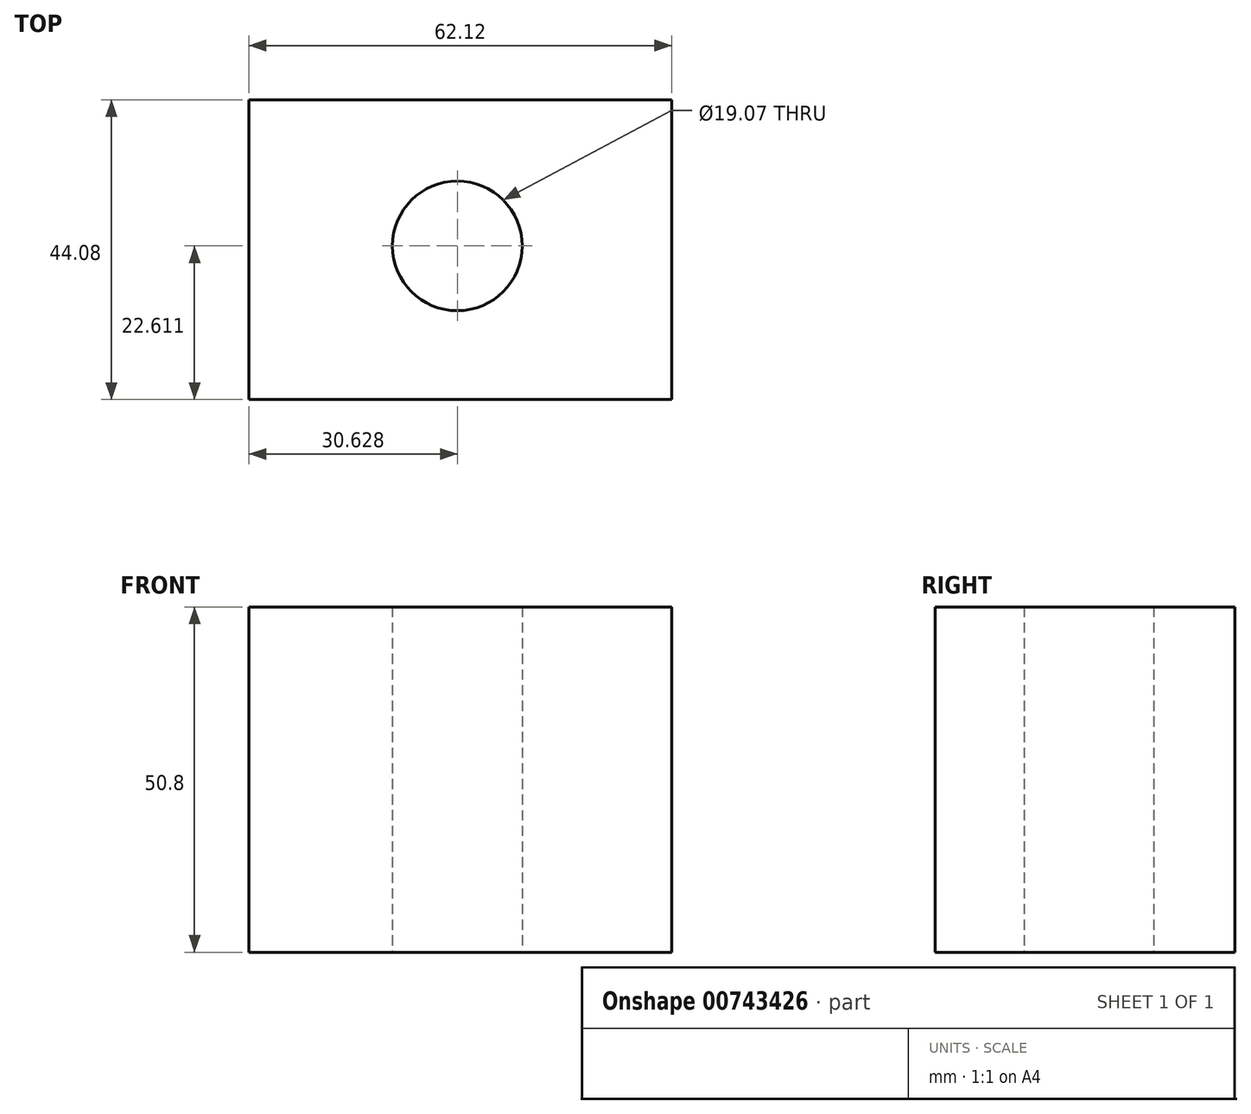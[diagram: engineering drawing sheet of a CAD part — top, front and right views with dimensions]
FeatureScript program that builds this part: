
annotation { "Feature Type Name" : "Feature", "Feature Type Description" : "" }
export const myFeature = defineFeature(function(context is Context, id is Id, definition is map)
    precondition{}
    {
        {
            var Q0;
            Q0=qCreatedBy(makeId("Top.planeOp"),FACE);
            var sketch = newSketch(context, id + "F0", { "sketchPlane" : qUnion([Q0])});
            skLineSegment(sketch, "E0.bottom", {"start": v(-71.15, 46.66) * mm, "end": v(-9.03, 46.66) * mm});
            skLineSegment(sketch, "E0.top", {"start": v(-71.15, 2.58) * mm, "end": v(-9.03, 2.58) * mm});
            skLineSegment(sketch, "E0.left", {"start": v(-71.15, 46.66) * mm, "end": v(-71.15, 2.58) * mm});
            skLineSegment(sketch, "E0.right", {"start": v(-9.03, 46.66) * mm, "end": v(-9.03, 2.58) * mm});
            skCircle(sketch, "E1", {"center": v(-40.52, 25.2) * mm, "radius": 9.53 * mm});
            skSolve(sketch);
        }
        {
            var Q0;
            Q0=makeQuery(id+"F0.imprint","IMPRINT",FACE,{"disambiguationData":[TD([[makeQuery(id+"F0.imprint","IMPRINT",EDGE,{"derivedFrom":sQuery(id+"F0.wireOp",EDGE,"E0.bottom")}),-1.0]])]});
            extrude(context, id + "F1", {"entities" : qUnion([Q0]), "depth" : 50.8 * mm, "offsetDistance" : 25.4 * mm});
        }
    });
